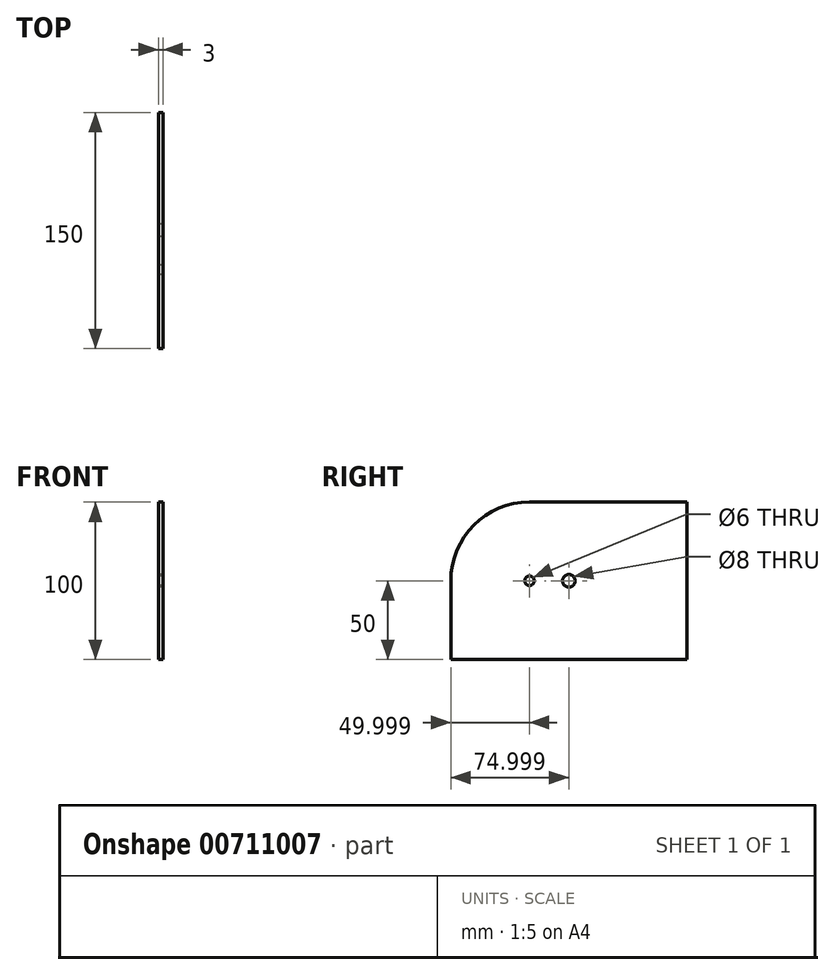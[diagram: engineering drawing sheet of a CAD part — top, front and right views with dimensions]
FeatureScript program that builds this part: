
annotation { "Feature Type Name" : "Feature", "Feature Type Description" : "" }
export const myFeature = defineFeature(function(context is Context, id is Id, definition is map)
    precondition{}
    {
        {
            var Q0;
            Q0=qCreatedBy(makeId("Right.planeOp"),FACE);
            var sketch = newSketch(context, id + "F0", { "sketchPlane" : qUnion([Q0])});
            skLineSegment(sketch, "E0.bottom", {"start": v(0.86, 113.83) * mm, "end": v(100.86, 113.83) * mm});
            skLineSegment(sketch, "E0.top", {"start": v(-49.14, 13.83) * mm, "end": v(100.86, 13.83) * mm});
            skLineSegment(sketch, "E0.left", {"start": v(-49.14, 63.83) * mm, "end": v(-49.14, 13.83) * mm});
            skLineSegment(sketch, "E0.right", {"start": v(100.86, 113.83) * mm, "end": v(100.86, 13.83) * mm});
            skPoint(sketch, "E1.visualSharp", {"position": v(-49.14, 113.83) * mm});
            skArc(sketch, "E1.filletArc", {"start": v(0.86, 113.83) * mm, "mid": v(-34.5, 99.19) * mm, "end": v(-49.14, 63.83) * mm});
            skCircle(sketch, "E2", {"center": v(0.86, 63.83) * mm, "radius": 3 * mm});
            skCircle(sketch, "E3", {"center": v(25.86, 63.83) * mm, "radius": 4 * mm});
            skSolve(sketch);
        }
        {
            var Q0;
            Q0=makeQuery(id+"F0.imprint","IMPRINT",FACE,{"disambiguationData":[TD([[makeQuery(id+"F0.imprint","IMPRINT",EDGE,{"derivedFrom":sQuery(id+"F0.wireOp",EDGE,"E0.bottom")}),-1.0]])]});
            extrude(context, id + "F1", {"entities" : qUnion([Q0]), "depth" : 3 * mm, "offsetDistance" : 25 * mm});
        }
    });
